# Revit family: Kulture Quoll Configurator
name_source: partatom
category: Furniture
units: mm (PartAtom-declared; Revit-internal decimal feet)

## family parameters
Always vertical = Yes
Cut with Voids When Loaded = No
OmniClass Number = 23.40.20.00
OmniClass Title = General Furniture and Specialties
Room Calculation Point = No
Shared = No
Work Plane-Based = Yes

## types (11) — shared parameters
1st Level Box 1 = Yes
Assembly Code = E2020200
Depth = 400 mm  [stored 1.31234 ft]
Foot = Gresham - BLACK PLASTIC
Frame = Gresham - BLACK METAL
Height = 400 mm  [stored 1.31234 ft]
Manufacturer = Gresham Office Furniture
Range = KULTURE QUOLL
Table Top = Gresham - CONCRETE
URL = www.gof.co.uk
Width = 400 mm  [stored 1.31234 ft]
zero-valued in all types: Default Elevation

## per-type parameters (varying)
| type | 1st Level Box 2 | 1st Level Box 3 | 2nd Level Box 1 | 2nd Level Box 2 | 2nd Level Box 3 | 3rd Level Box 1 | 3rd Level Box 2 | 3rd Level Box 3 | 4th Level Box 1 | 4th Level Box 2 | 4th Level Box 3 | 5th Level Box 1 | 5th Level Box 2 | 5th Level Box 3 | Product Code |
| Storage - 1 Wide x 1 High Unit | No | No | No | No | No | No | No | No | No | No | No | No | No | No | KQ1W1H |
| Storage - 2 Wide x 2 High Step Unit | Yes | No | Yes | No | No | No | No | No | No | No | No | No | No | No | KQ2W2HST |
| Storage - 2 Wide x 2 High Unit | Yes | No | Yes | Yes | No | No | No | No | No | No | No | No | No | No | KQ2W2H |
| Storage - 3 Wide x 3 High Step Unit | Yes | Yes | Yes | Yes | No | Yes | No | No | No | No | No | No | No | No | KQ3W3HST |
| Storage - 3 Wide x 4 High Step Unit | Yes | Yes | Yes | Yes | No | Yes | No | No | Yes | No | No | No | No | No | KQ3W4HST |
| Storage - 3 Wide x 5 High Step Unit | Yes | Yes | Yes | Yes | Yes | Yes | Yes | No | Yes | No | No | Yes | No | No | KQ3WHST |
| Storage - 3 Wide x 1 High Unit | Yes | Yes | No | No | No | No | No | No | No | No | No | No | No | No | KQ3W1H |
| Storage - 3 Wide x 2 High Unit | Yes | Yes | Yes | Yes | Yes | No | No | No | No | No | No | No | No | No | KQW3W2H |
| Storage - 3 Wide x 3 High Unit | Yes | Yes | Yes | Yes | Yes | Yes | Yes | Yes | No | No | No | No | No | No | KQ3W3H |
| Storage - 3 Wide x 4 High Unit | Yes | Yes | Yes | Yes | Yes | Yes | Yes | Yes | Yes | Yes | Yes | No | No | No | KQ3W4H |
| Storage - 3 Wide x 5 High Unit | Yes | Yes | Yes | Yes | Yes | Yes | Yes | Yes | Yes | Yes | Yes | Yes | Yes | Yes | KQ3W5H |

note: [stored X ft] marks values corroborated as IEEE doubles in the binary element streams (Revit-internal decimal feet)

## geometry (parser evidence)
native form markers: Sweep x13
no freeform markers — native parametric forms only
